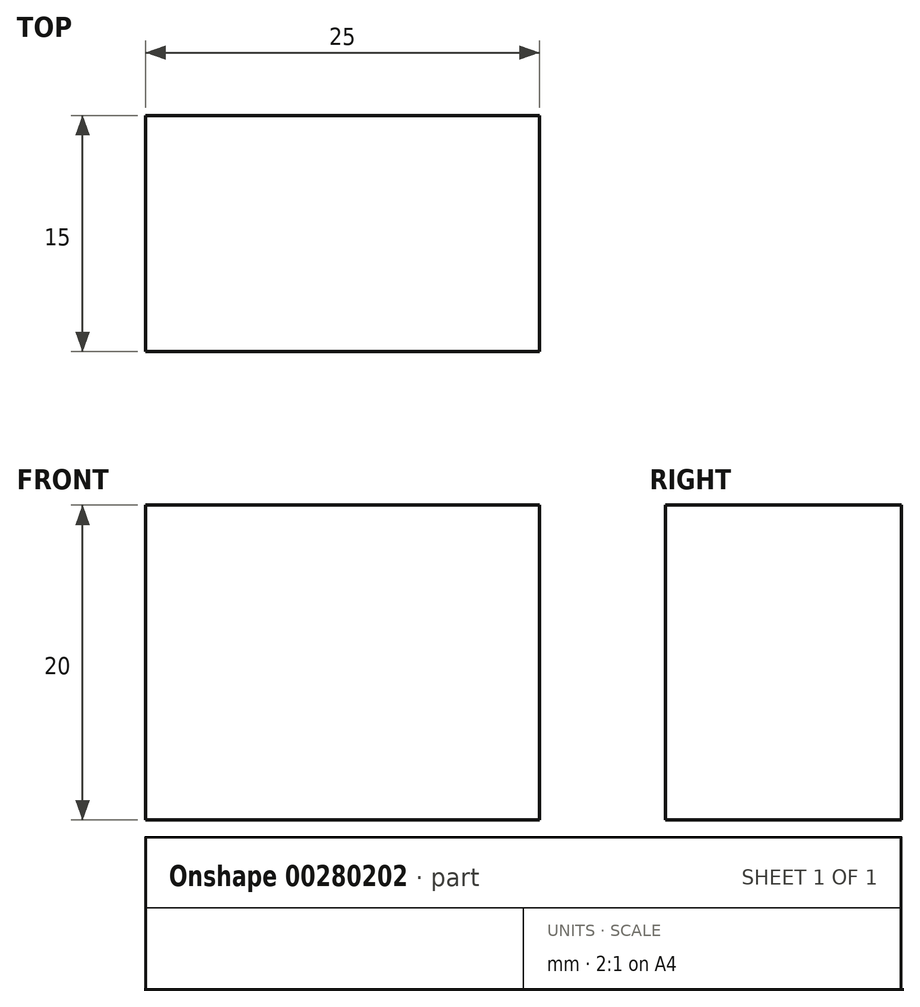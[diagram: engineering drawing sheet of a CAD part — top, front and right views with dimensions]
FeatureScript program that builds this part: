
annotation { "Feature Type Name" : "Feature", "Feature Type Description" : "" }
export const myFeature = defineFeature(function(context is Context, id is Id, definition is map)
    precondition{}
    {
        {
            var Q0;
            Q0=qCreatedBy(makeId("Front.planeOp"),FACE);
            var sketch = newSketch(context, id + "F0", { "sketchPlane" : qUnion([Q0])});
            skLineSegment(sketch, "E0.bottom", {"start": v(0, 0) * mm, "end": v(25, 0) * mm});
            skLineSegment(sketch, "E0.top", {"start": v(0, 20) * mm, "end": v(25, 20) * mm});
            skLineSegment(sketch, "E0.left", {"start": v(0, 0) * mm, "end": v(0, 20) * mm});
            skLineSegment(sketch, "E0.right", {"start": v(25, 0) * mm, "end": v(25, 20) * mm});
            skSolve(sketch);
        }
        {
            var Q0;
            Q0=makeQuery(id+"F0.imprint","IMPRINT",FACE,{"disambiguationData":[TD([[makeQuery(id+"F0.imprint","IMPRINT",EDGE,{"derivedFrom":sQuery(id+"F0.wireOp",EDGE,"E0.bottom")}),1.0]])]});
            extrude(context, id + "F1", {"entities" : qUnion([Q0]), "oppositeDirection" : true, "depth" : 15 * mm});
        }
    });
